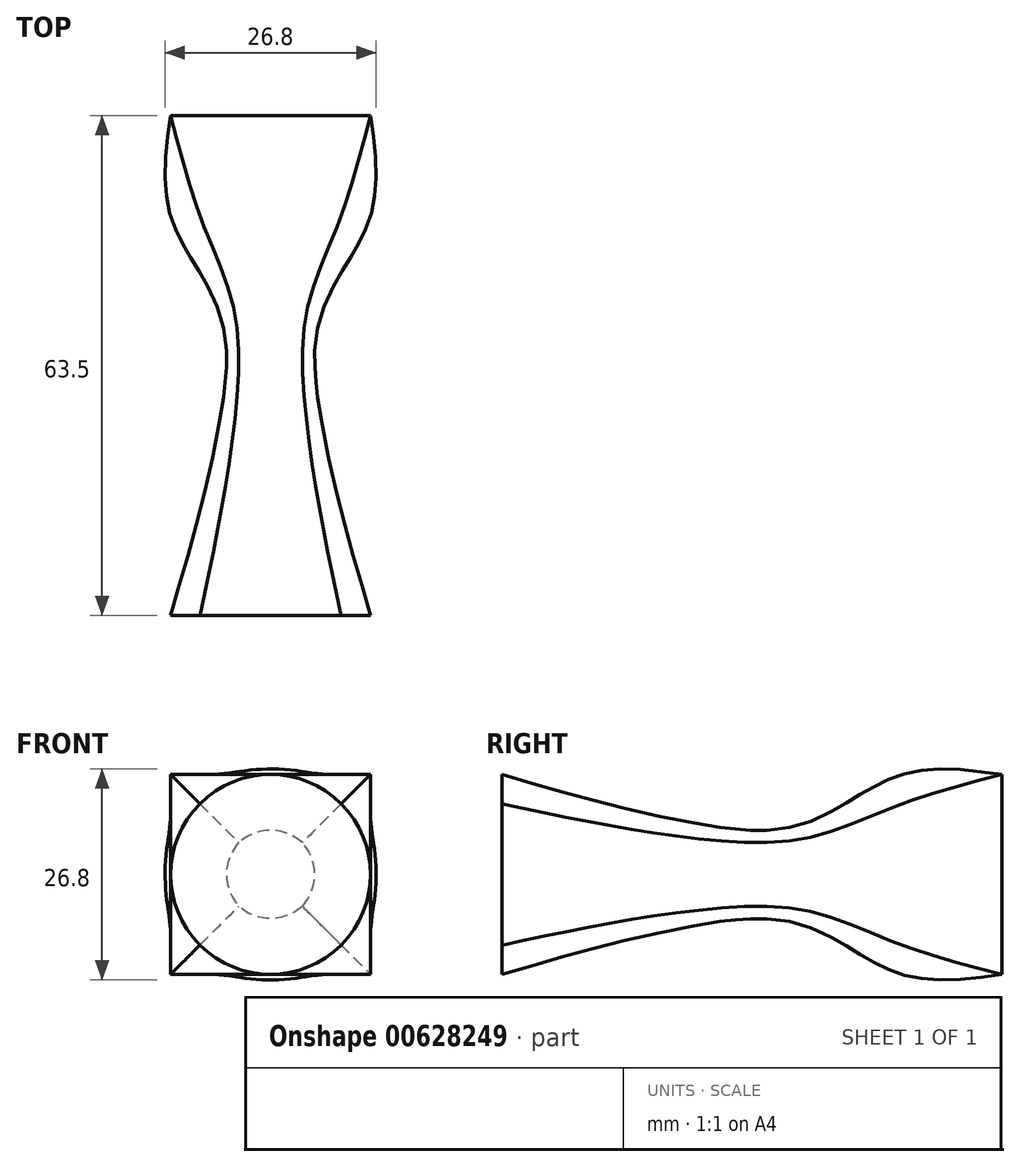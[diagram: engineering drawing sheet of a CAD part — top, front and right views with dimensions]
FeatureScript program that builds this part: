
annotation { "Feature Type Name" : "Feature", "Feature Type Description" : "" }
export const myFeature = defineFeature(function(context is Context, id is Id, definition is map)
    precondition{}
    {
        {
            var Q0;
            Q0=qCreatedBy(makeId("Front.planeOp"),FACE);
            var sketch = newSketch(context, id + "F0", { "sketchPlane" : qUnion([Q0])});
            skCircle(sketch, "E0", {"center": v(0, 0) * mm, "radius": 12.7 * mm});
            skSolve(sketch);
        }
        {
            var Q0;
            Q0=qCreatedBy(makeId("Front.planeOp"),FACE);
            cPlane(context, id + "F1", {"entities" : qUnion([Q0]), "cplaneType" : CPlaneType.OFFSET, "offset" : 12.7 * mm, "width" : 152.4 * mm, "height" : 152.4 * mm});
        }
        {
            var Q0;
            Q0=qCreatedBy(id+"F1.planeOp",FACE);
            var sketch = newSketch(context, id + "F2", { "sketchPlane" : qUnion([Q0])});
            skCircle(sketch, "E1", {"center": v(0, 0) * mm, "radius": 6.35 * mm});
            skSolve(sketch);
        }
        {
            var Q0;
            Q0=qCreatedBy(id+"F1.planeOp",FACE);
            cPlane(context, id + "F3", {"entities" : qUnion([Q0]), "cplaneType" : CPlaneType.OFFSET, "offset" : 12.7 * mm, "width" : 152.4 * mm, "height" : 152.4 * mm});
        }
        {
            var Q0;
            Q0=qCreatedBy(id+"F3.planeOp",FACE);
            var sketch = newSketch(context, id + "F4", { "sketchPlane" : qUnion([Q0])});
            skCircle(sketch, "E2", {"center": v(0, 0) * mm, "radius": 6.35 * mm});
            skSolve(sketch);
        }
        {
            var Q0;
            Q0=qCreatedBy(id+"F3.planeOp",FACE);
            cPlane(context, id + "F5", {"entities" : qUnion([Q0]), "cplaneType" : CPlaneType.OFFSET, "offset" : 25.4 * mm, "width" : 152.4 * mm, "height" : 152.4 * mm});
        }
        {
            var Q0;
            Q0=qCreatedBy(id+"F5.planeOp",FACE);
            var sketch = newSketch(context, id + "F6", { "sketchPlane" : qUnion([Q0])});
            skCircle(sketch, "E3", {"center": v(0, 0) * mm, "radius": 12.7 * mm});
            skSolve(sketch);
        }
        {
            var Q0;
            Q0=qCreatedBy(makeId("Front.planeOp"),FACE);
            cPlane(context, id + "F7", {"entities" : qUnion([Q0]), "cplaneType" : CPlaneType.OFFSET, "offset" : 12.7 * mm, "oppositeDirection" : true, "width" : 152.4 * mm, "height" : 152.4 * mm});
        }
        {
            var Q0;
            Q0=qCreatedBy(id+"F7.planeOp",FACE);
            var sketch = newSketch(context, id + "F8", { "sketchPlane" : qUnion([Q0])});
            skLineSegment(sketch, "E4.bottom", {"start": v(-12.7, -12.7) * mm, "end": v(12.7, -12.7) * mm});
            skLineSegment(sketch, "E4.top", {"start": v(-12.7, 12.7) * mm, "end": v(12.7, 12.7) * mm});
            skLineSegment(sketch, "E4.left", {"start": v(-12.7, -12.7) * mm, "end": v(-12.7, 12.7) * mm});
            skLineSegment(sketch, "E4.right", {"start": v(12.7, -12.7) * mm, "end": v(12.7, 12.7) * mm});
            skPoint(sketch, "E4.middle", {"position": v(0, 0) * mm});
            skSolve(sketch);
        }
        {
            var Q0;
            Q0 = qSketchRegion(id + "F6", true);
            var Q1;
            Q1 = qSketchRegion(id + "F4", true);
            var Q2;
            Q2 = qSketchRegion(id + "F2", true);
            var Q3;
            Q3 = qSketchRegion(id + "F0", true);
            var Q4;
            Q4 = qSketchRegion(id + "F8", true);
            loft(context, id + "F9", {"sheetProfilesArray" : [{ "sheetProfileEntities" : qUnion([Q0]) }, { "sheetProfileEntities" : qUnion([Q1]) }, { "sheetProfileEntities" : qUnion([Q2]) }, { "sheetProfileEntities" : qUnion([Q3]) }, { "sheetProfileEntities" : qUnion([Q4]) }]});
        }
        {
            var Q0;
            Q0=qCreatedBy(id+"F7.planeOp",FACE);
            cPlane(context, id + "F10", {"entities" : qUnion([Q0]), "cplaneType" : CPlaneType.OFFSET, "offset" : 38.1 * mm, "oppositeDirection" : true, "width" : 152.4 * mm, "height" : 152.4 * mm});
        }
    });
